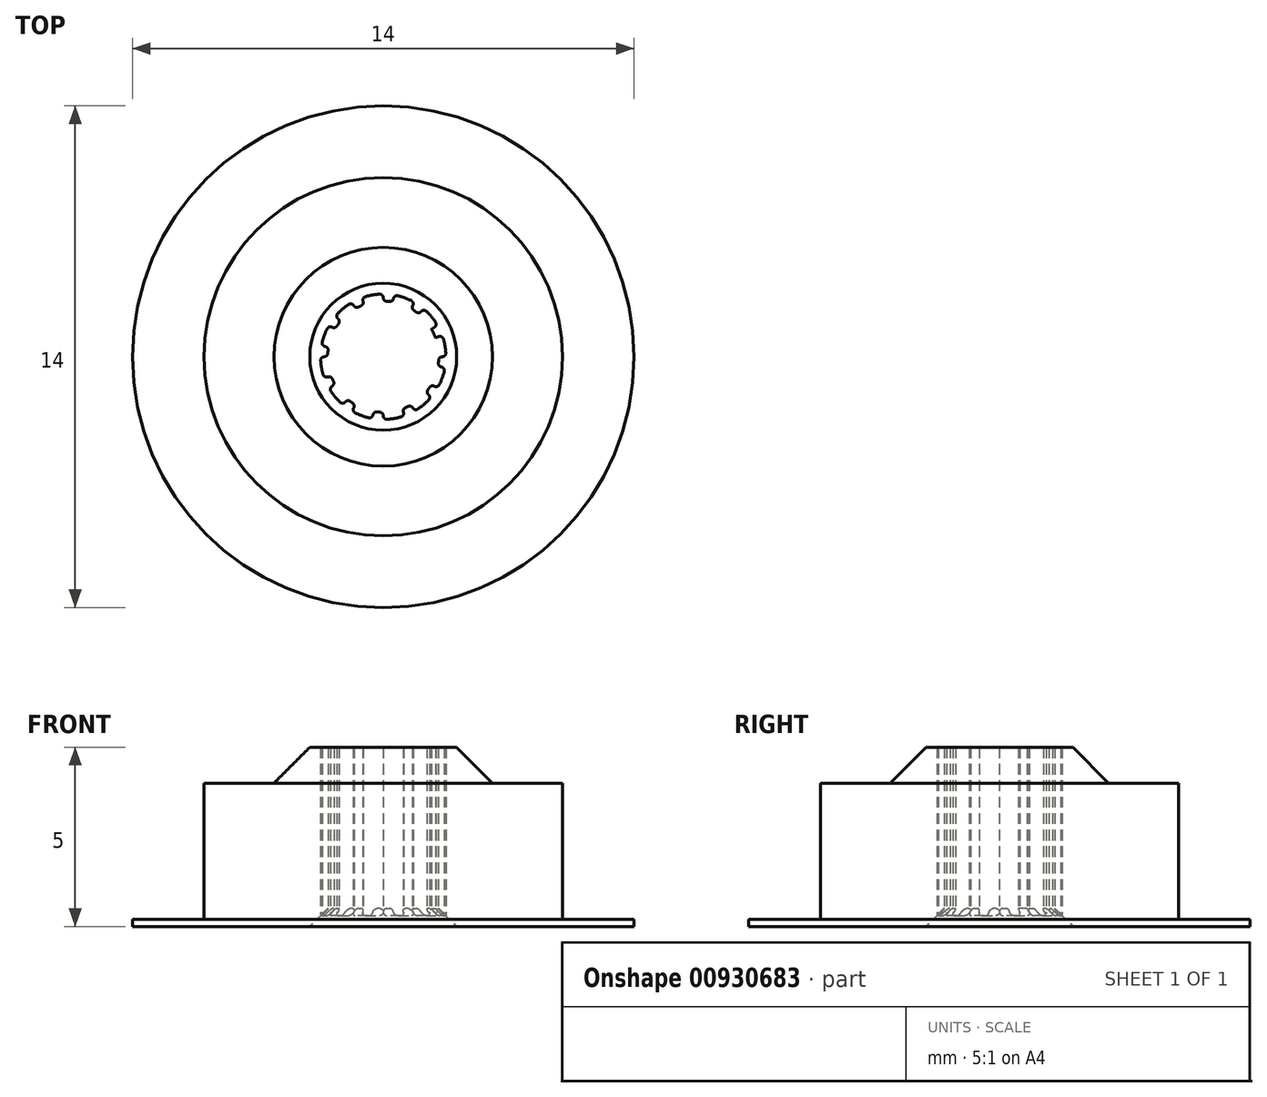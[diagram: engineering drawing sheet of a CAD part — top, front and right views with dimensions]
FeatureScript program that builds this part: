
annotation { "Feature Type Name" : "Feature", "Feature Type Description" : "" }
export const myFeature = defineFeature(function(context is Context, id is Id, definition is map)
    precondition{}
    {
        {
            var Q0;
            Q0=qCreatedBy(makeId("Front.planeOp"),FACE);
            var sketch = newSketch(context, id + "F0", { "sketchPlane" : qUnion([Q0])});
            skLineSegment(sketch, "E0", {"start": v(0, 0) * mm, "end": v(0, 10) * mm, "construction": true});
            skLineSegment(sketch, "E1", {"start": v(1.55, 5) * mm, "end": v(2.05, 5) * mm});
            skLineSegment(sketch, "E2", {"start": v(2.05, 5) * mm, "end": v(3.05, 4) * mm});
            skLineSegment(sketch, "E3", {"start": v(3.05, 4) * mm, "end": v(5, 4) * mm});
            skLineSegment(sketch, "E4", {"start": v(5, 4) * mm, "end": v(5, 0) * mm});
            skLineSegment(sketch, "E5", {"start": v(5, 0) * mm, "end": v(2.05, 0) * mm});
            skLineSegment(sketch, "E6", {"start": v(1.55, 0.5) * mm, "end": v(1.55, 5) * mm});
            skLineSegment(sketch, "E7", {"start": v(2.05, 0) * mm, "end": v(1.55, 0.5) * mm});
            skSolve(sketch);
        }
        {
            var Q0;
            Q0=qSketchRegion(id+"F0",true);
            var Q1;
            Q1=sQuery(id+"F0.wireOp",EDGE,"E0");
            revolve(context, id + "F1", {"entities" : qUnion([Q0]), "axis" : qUnion([Q1]), "revolveType" : RevolveType.FULL});
        }
        {
            var Q0;
            Q0=makeQuery(id+"F1.opRevolve","SWEPT_FACE",FACE,{"disambiguationData":[OSD([sQuery(id+"F0.wireOp",EDGE,"E5")])]});
            var sketch = newSketch(context, id + "F2", { "sketchPlane" : qUnion([Q0])});
            skCircle(sketch, "E8", {"center": v(0, 0) * mm, "radius": 1.5 * mm, "construction": true});
            skArc(sketch, "E9", {"start": v(-1.72, -0.3) * mm, "mid": v(-1.64, -0.6) * mm, "end": v(-1.52, -0.87) * mm});
            skArc(sketch, "E10", {"start": v(-1.34, -0.78) * mm, "mid": v(-1.27, -0.89) * mm, "end": v(-1.19, -1) * mm});
            skLineSegment(sketch, "E11", {"start": v(-1.75, 0) * mm, "end": v(-1.55, 0) * mm});
            skLineSegment(sketch, "E12", {"start": v(-1.72, -0.3) * mm, "end": v(-1.53, -0.27) * mm});
            skLineSegment(sketch, "E13.1.0", {"start": v(-1.34, -1.12) * mm, "end": v(-1.19, -1) * mm});
            skLineSegment(sketch, "E13.1.1", {"start": v(-1.52, -0.88) * mm, "end": v(-1.34, -0.78) * mm});
            skLineSegment(sketch, "E13.2.0", {"start": v(-0.6, -1.64) * mm, "end": v(-0.53, -1.46) * mm});
            skLineSegment(sketch, "E13.2.1", {"start": v(-0.88, -1.52) * mm, "end": v(-0.78, -1.34) * mm});
            skLineSegment(sketch, "E13.3.0", {"start": v(0.3, -1.72) * mm, "end": v(0.27, -1.53) * mm});
            skLineSegment(sketch, "E13.3.1", {"start": v(0, -1.75) * mm, "end": v(0, -1.55) * mm});
            skLineSegment(sketch, "E13.4.0", {"start": v(1.12, -1.34) * mm, "end": v(1, -1.19) * mm});
            skLineSegment(sketch, "E13.4.1", {"start": v(0.88, -1.52) * mm, "end": v(0.78, -1.34) * mm});
            skLineSegment(sketch, "E13.5.0", {"start": v(1.64, -0.6) * mm, "end": v(1.46, -0.53) * mm});
            skLineSegment(sketch, "E13.5.1", {"start": v(1.52, -0.88) * mm, "end": v(1.34, -0.78) * mm});
            skLineSegment(sketch, "E13.6.0", {"start": v(1.72, 0.3) * mm, "end": v(1.53, 0.27) * mm});
            skLineSegment(sketch, "E13.6.1", {"start": v(1.75, 0) * mm, "end": v(1.55, 0) * mm});
            skLineSegment(sketch, "E13.7.0", {"start": v(1.34, 1.12) * mm, "end": v(1.19, 1) * mm});
            skLineSegment(sketch, "E13.7.1", {"start": v(1.52, 0.88) * mm, "end": v(1.34, 0.78) * mm});
            skLineSegment(sketch, "E13.8.0", {"start": v(0.6, 1.64) * mm, "end": v(0.53, 1.46) * mm});
            skLineSegment(sketch, "E13.8.1", {"start": v(0.88, 1.52) * mm, "end": v(0.78, 1.34) * mm});
            skLineSegment(sketch, "E13.9.0", {"start": v(-0.3, 1.72) * mm, "end": v(-0.27, 1.53) * mm});
            skLineSegment(sketch, "E13.9.1", {"start": v(0, 1.75) * mm, "end": v(0, 1.55) * mm});
            skLineSegment(sketch, "E13.10.0", {"start": v(-1.12, 1.34) * mm, "end": v(-1, 1.19) * mm});
            skLineSegment(sketch, "E13.10.1", {"start": v(-0.87, 1.52) * mm, "end": v(-0.77, 1.34) * mm});
            skLineSegment(sketch, "E13.11.0", {"start": v(-1.64, 0.6) * mm, "end": v(-1.46, 0.53) * mm});
            skLineSegment(sketch, "E13.11.1", {"start": v(-1.52, 0.88) * mm, "end": v(-1.34, 0.78) * mm});
            skArc(sketch, "E14.trimOffspring", {"start": v(-1.34, -1.12) * mm, "mid": v(-1.12, -1.34) * mm, "end": v(-0.88, -1.52) * mm});
            skArc(sketch, "E15.trimOffspring", {"start": v(-0.6, -1.64) * mm, "mid": v(-0.3, -1.72) * mm, "end": v(0, -1.75) * mm});
            skArc(sketch, "E16.trimOffspring", {"start": v(0.3, -1.72) * mm, "mid": v(0.6, -1.64) * mm, "end": v(0.87, -1.52) * mm});
            skArc(sketch, "E17.trimOffspring", {"start": v(1.12, -1.34) * mm, "mid": v(1.34, -1.12) * mm, "end": v(1.52, -0.88) * mm});
            skArc(sketch, "E18.trimOffspring", {"start": v(1.64, -0.6) * mm, "mid": v(1.72, -0.3) * mm, "end": v(1.75, 0) * mm});
            skArc(sketch, "E19.trimOffspring", {"start": v(1.72, 0.3) * mm, "mid": v(1.64, 0.6) * mm, "end": v(1.52, 0.87) * mm});
            skArc(sketch, "E20.trimOffspring", {"start": v(1.34, 1.12) * mm, "mid": v(1.12, 1.34) * mm, "end": v(0.88, 1.52) * mm});
            skArc(sketch, "E21.trimOffspring", {"start": v(0.6, 1.64) * mm, "mid": v(0.3, 1.72) * mm, "end": v(0, 1.75) * mm});
            skArc(sketch, "E22.trimOffspring", {"start": v(-0.3, 1.72) * mm, "mid": v(-0.6, 1.64) * mm, "end": v(-0.87, 1.52) * mm});
            skArc(sketch, "E23.trimOffspring", {"start": v(-1.12, 1.34) * mm, "mid": v(-1.34, 1.12) * mm, "end": v(-1.52, 0.88) * mm});
            skArc(sketch, "E24.trimOffspring", {"start": v(-1.64, 0.6) * mm, "mid": v(-1.72, 0.3) * mm, "end": v(-1.75, 0) * mm});
            skArc(sketch, "E25.trimOffspring", {"start": v(-0.78, -1.34) * mm, "mid": v(-0.66, -1.4) * mm, "end": v(-0.53, -1.46) * mm});
            skArc(sketch, "E26.trimOffspring", {"start": v(0, -1.55) * mm, "mid": v(0.14, -1.54) * mm, "end": v(0.27, -1.53) * mm});
            skArc(sketch, "E27.trimOffspring", {"start": v(0.77, -1.34) * mm, "mid": v(0.89, -1.27) * mm, "end": v(1, -1.19) * mm});
            skArc(sketch, "E28.trimOffspring", {"start": v(1.34, -0.78) * mm, "mid": v(1.4, -0.66) * mm, "end": v(1.46, -0.53) * mm});
            skArc(sketch, "E29.trimOffspring", {"start": v(1.55, 0) * mm, "mid": v(1.54, 0.14) * mm, "end": v(1.53, 0.27) * mm});
            skArc(sketch, "E30.trimOffspring", {"start": v(1.34, 0.77) * mm, "mid": v(1.27, 0.89) * mm, "end": v(1.19, 1) * mm});
            skArc(sketch, "E31.trimOffspring", {"start": v(0.78, 1.34) * mm, "mid": v(0.66, 1.4) * mm, "end": v(0.53, 1.46) * mm});
            skArc(sketch, "E32.trimOffspring", {"start": v(0, 1.55) * mm, "mid": v(-0.14, 1.54) * mm, "end": v(-0.27, 1.53) * mm});
            skArc(sketch, "E33.trimOffspring", {"start": v(-0.77, 1.34) * mm, "mid": v(-0.89, 1.27) * mm, "end": v(-1, 1.19) * mm});
            skArc(sketch, "E34.trimOffspring", {"start": v(-1.34, 0.78) * mm, "mid": v(-1.4, 0.66) * mm, "end": v(-1.46, 0.53) * mm});
            skArc(sketch, "E35.trimOffspring", {"start": v(-1.55, 0) * mm, "mid": v(-1.54, -0.14) * mm, "end": v(-1.53, -0.27) * mm});
            skSolve(sketch);
        }
        {
            var Q0;
            Q0=qSketchRegion(id+"F2",true);
            var Q1;
            Q1=makeQuery(id+"F1.opRevolve","SWEPT_FACE",FACE,{"disambiguationData":[OSD([sQuery(id+"F0.wireOp",EDGE,"E1")])]});
            extrude(context, id + "F3", {"entities" : qUnion([Q0]), "operationType" : NewBodyOperationType.REMOVE, "endBound" : BoundingType.UP_TO_SURFACE, "oppositeDirection" : true, "depth" : 25 * mm, "endBoundEntityFace" : qUnion([Q1]), "offsetDistance" : 25 * mm});
        }
        {
            var Q0;
            Q0=makeQuery(id+"F3.boolean.opBoolean","COPY",EDGE,{"derivedFrom":makeQuery(id+"F3.opExtrude","SWEPT_EDGE",EDGE,{"disambiguationData":[OSD([sQuery(id+"F2.wireOp",EDGE,"E13.4.0"),sQuery(id+"F2.wireOp",EDGE,"E17.trimOffspring")])]})});
            var Q1;
            Q1=makeQuery(id+"F3.boolean.opBoolean","COPY",EDGE,{"derivedFrom":makeQuery(id+"F3.opExtrude","SWEPT_EDGE",EDGE,{"disambiguationData":[OSD([sQuery(id+"F2.wireOp",EDGE,"E13.4.1"),sQuery(id+"F2.wireOp",EDGE,"E16.trimOffspring")])]})});
            var Q2;
            Q2=makeQuery(id+"F3.boolean.opBoolean","COPY",EDGE,{"derivedFrom":makeQuery(id+"F3.opExtrude","SWEPT_EDGE",EDGE,{"disambiguationData":[OSD([sQuery(id+"F2.wireOp",EDGE,"E13.4.0"),sQuery(id+"F2.wireOp",EDGE,"E27.trimOffspring")])]})});
            var Q3;
            Q3=makeQuery(id+"F3.boolean.opBoolean","COPY",EDGE,{"derivedFrom":makeQuery(id+"F3.opExtrude","SWEPT_EDGE",EDGE,{"disambiguationData":[OSD([sQuery(id+"F2.wireOp",EDGE,"E13.4.1"),sQuery(id+"F2.wireOp",EDGE,"E27.trimOffspring")])]})});
            var Q4;
            Q4=makeQuery(id+"F3.boolean.opBoolean","COPY",EDGE,{"derivedFrom":makeQuery(id+"F3.opExtrude","SWEPT_EDGE",EDGE,{"disambiguationData":[OSD([sQuery(id+"F2.wireOp",EDGE,"E13.3.0"),sQuery(id+"F2.wireOp",EDGE,"E16.trimOffspring")])]})});
            var Q5;
            Q5=makeQuery(id+"F3.boolean.opBoolean","COPY",EDGE,{"derivedFrom":makeQuery(id+"F3.opExtrude","SWEPT_EDGE",EDGE,{"disambiguationData":[OSD([sQuery(id+"F2.wireOp",EDGE,"E13.3.0"),sQuery(id+"F2.wireOp",EDGE,"E26.trimOffspring")])]})});
            var Q6;
            Q6=makeQuery(id+"F3.boolean.opBoolean","COPY",EDGE,{"derivedFrom":makeQuery(id+"F3.opExtrude","SWEPT_EDGE",EDGE,{"disambiguationData":[OSD([sQuery(id+"F2.wireOp",EDGE,"E13.3.1"),sQuery(id+"F2.wireOp",EDGE,"E26.trimOffspring")])]})});
            var Q7;
            Q7=makeQuery(id+"F3.boolean.opBoolean","COPY",EDGE,{"derivedFrom":makeQuery(id+"F3.opExtrude","SWEPT_EDGE",EDGE,{"disambiguationData":[OSD([sQuery(id+"F2.wireOp",EDGE,"E13.3.1"),sQuery(id+"F2.wireOp",EDGE,"E15.trimOffspring")])]})});
            var Q8;
            Q8=makeQuery(id+"F3.boolean.opBoolean","COPY",EDGE,{"derivedFrom":makeQuery(id+"F3.opExtrude","SWEPT_EDGE",EDGE,{"disambiguationData":[OSD([sQuery(id+"F2.wireOp",EDGE,"E13.2.0"),sQuery(id+"F2.wireOp",EDGE,"E15.trimOffspring")])]})});
            var Q9;
            Q9=makeQuery(id+"F3.boolean.opBoolean","COPY",EDGE,{"derivedFrom":makeQuery(id+"F3.opExtrude","SWEPT_EDGE",EDGE,{"disambiguationData":[OSD([sQuery(id+"F2.wireOp",EDGE,"E13.2.0"),sQuery(id+"F2.wireOp",EDGE,"E25.trimOffspring")])]})});
            var Q10;
            Q10=makeQuery(id+"F3.boolean.opBoolean","COPY",EDGE,{"derivedFrom":makeQuery(id+"F3.opExtrude","SWEPT_EDGE",EDGE,{"disambiguationData":[OSD([sQuery(id+"F2.wireOp",EDGE,"E13.2.1"),sQuery(id+"F2.wireOp",EDGE,"E25.trimOffspring")])]})});
            var Q11;
            Q11=makeQuery(id+"F3.boolean.opBoolean","COPY",EDGE,{"derivedFrom":makeQuery(id+"F3.opExtrude","SWEPT_EDGE",EDGE,{"disambiguationData":[OSD([sQuery(id+"F2.wireOp",EDGE,"E13.2.1"),sQuery(id+"F2.wireOp",EDGE,"E14.trimOffspring")])]})});
            var Q12;
            Q12=makeQuery(id+"F3.boolean.opBoolean","COPY",EDGE,{"derivedFrom":makeQuery(id+"F3.opExtrude","SWEPT_EDGE",EDGE,{"disambiguationData":[OSD([sQuery(id+"F2.wireOp",EDGE,"E13.1.0"),sQuery(id+"F2.wireOp",EDGE,"E14.trimOffspring")])]})});
            var Q13;
            Q13=makeQuery(id+"F3.boolean.opBoolean","COPY",EDGE,{"derivedFrom":makeQuery(id+"F3.opExtrude","SWEPT_EDGE",EDGE,{"disambiguationData":[OSD([sQuery(id+"F2.wireOp",EDGE,"E10"),sQuery(id+"F2.wireOp",EDGE,"E13.1.0")])]})});
            var Q14;
            Q14=makeQuery(id+"F3.boolean.opBoolean","COPY",EDGE,{"derivedFrom":makeQuery(id+"F3.opExtrude","SWEPT_EDGE",EDGE,{"disambiguationData":[OSD([sQuery(id+"F2.wireOp",EDGE,"E10"),sQuery(id+"F2.wireOp",EDGE,"E13.1.1")])]})});
            var Q15;
            Q15=makeQuery(id+"F3.boolean.opBoolean","COPY",EDGE,{"derivedFrom":makeQuery(id+"F3.opExtrude","SWEPT_EDGE",EDGE,{"disambiguationData":[OSD([sQuery(id+"F2.wireOp",EDGE,"E9"),sQuery(id+"F2.wireOp",EDGE,"E13.1.1")])]})});
            var Q16;
            Q16=makeQuery(id+"F3.boolean.opBoolean","COPY",EDGE,{"derivedFrom":makeQuery(id+"F3.opExtrude","SWEPT_EDGE",EDGE,{"disambiguationData":[OSD([sQuery(id+"F2.wireOp",EDGE,"E9"),sQuery(id+"F2.wireOp",EDGE,"E12")])]})});
            var Q17;
            Q17=makeQuery(id+"F3.boolean.opBoolean","COPY",EDGE,{"derivedFrom":makeQuery(id+"F3.opExtrude","SWEPT_EDGE",EDGE,{"disambiguationData":[OSD([sQuery(id+"F2.wireOp",EDGE,"E12"),sQuery(id+"F2.wireOp",EDGE,"E35.trimOffspring")])]})});
            var Q18;
            Q18=makeQuery(id+"F3.boolean.opBoolean","COPY",EDGE,{"derivedFrom":makeQuery(id+"F3.opExtrude","SWEPT_EDGE",EDGE,{"disambiguationData":[OSD([sQuery(id+"F2.wireOp",EDGE,"E11"),sQuery(id+"F2.wireOp",EDGE,"E35.trimOffspring")])]})});
            var Q19;
            Q19=makeQuery(id+"F3.boolean.opBoolean","COPY",EDGE,{"derivedFrom":makeQuery(id+"F3.opExtrude","SWEPT_EDGE",EDGE,{"disambiguationData":[OSD([sQuery(id+"F2.wireOp",EDGE,"E11"),sQuery(id+"F2.wireOp",EDGE,"E24.trimOffspring")])]})});
            var Q20;
            Q20=makeQuery(id+"F3.boolean.opBoolean","COPY",EDGE,{"derivedFrom":makeQuery(id+"F3.opExtrude","SWEPT_EDGE",EDGE,{"disambiguationData":[OSD([sQuery(id+"F2.wireOp",EDGE,"E13.11.0"),sQuery(id+"F2.wireOp",EDGE,"E24.trimOffspring")])]})});
            var Q21;
            Q21=makeQuery(id+"F3.boolean.opBoolean","COPY",EDGE,{"derivedFrom":makeQuery(id+"F3.opExtrude","SWEPT_EDGE",EDGE,{"disambiguationData":[OSD([sQuery(id+"F2.wireOp",EDGE,"E13.11.0"),sQuery(id+"F2.wireOp",EDGE,"E34.trimOffspring")])]})});
            var Q22;
            Q22=makeQuery(id+"F3.boolean.opBoolean","COPY",EDGE,{"derivedFrom":makeQuery(id+"F3.opExtrude","SWEPT_EDGE",EDGE,{"disambiguationData":[OSD([sQuery(id+"F2.wireOp",EDGE,"E13.11.1"),sQuery(id+"F2.wireOp",EDGE,"E34.trimOffspring")])]})});
            var Q23;
            Q23=makeQuery(id+"F3.boolean.opBoolean","COPY",EDGE,{"derivedFrom":makeQuery(id+"F3.opExtrude","SWEPT_EDGE",EDGE,{"disambiguationData":[OSD([sQuery(id+"F2.wireOp",EDGE,"E13.11.1"),sQuery(id+"F2.wireOp",EDGE,"E23.trimOffspring")])]})});
            var Q24;
            Q24=makeQuery(id+"F3.boolean.opBoolean","COPY",EDGE,{"derivedFrom":makeQuery(id+"F3.opExtrude","SWEPT_EDGE",EDGE,{"disambiguationData":[OSD([sQuery(id+"F2.wireOp",EDGE,"E13.10.0"),sQuery(id+"F2.wireOp",EDGE,"E23.trimOffspring")])]})});
            var Q25;
            Q25=makeQuery(id+"F3.boolean.opBoolean","COPY",EDGE,{"derivedFrom":makeQuery(id+"F3.opExtrude","SWEPT_EDGE",EDGE,{"disambiguationData":[OSD([sQuery(id+"F2.wireOp",EDGE,"E13.10.0"),sQuery(id+"F2.wireOp",EDGE,"E33.trimOffspring")])]})});
            var Q26;
            Q26=makeQuery(id+"F3.boolean.opBoolean","COPY",EDGE,{"derivedFrom":makeQuery(id+"F3.opExtrude","SWEPT_EDGE",EDGE,{"disambiguationData":[OSD([sQuery(id+"F2.wireOp",EDGE,"E13.10.1"),sQuery(id+"F2.wireOp",EDGE,"E33.trimOffspring")])]})});
            var Q27;
            Q27=makeQuery(id+"F3.boolean.opBoolean","COPY",EDGE,{"derivedFrom":makeQuery(id+"F3.opExtrude","SWEPT_EDGE",EDGE,{"disambiguationData":[OSD([sQuery(id+"F2.wireOp",EDGE,"E13.10.1"),sQuery(id+"F2.wireOp",EDGE,"E22.trimOffspring")])]})});
            var Q28;
            Q28=makeQuery(id+"F3.boolean.opBoolean","COPY",EDGE,{"derivedFrom":makeQuery(id+"F3.opExtrude","SWEPT_EDGE",EDGE,{"disambiguationData":[OSD([sQuery(id+"F2.wireOp",EDGE,"E13.9.0"),sQuery(id+"F2.wireOp",EDGE,"E22.trimOffspring")])]})});
            var Q29;
            Q29=makeQuery(id+"F3.boolean.opBoolean","COPY",EDGE,{"derivedFrom":makeQuery(id+"F3.opExtrude","SWEPT_EDGE",EDGE,{"disambiguationData":[OSD([sQuery(id+"F2.wireOp",EDGE,"E13.9.0"),sQuery(id+"F2.wireOp",EDGE,"E32.trimOffspring")])]})});
            var Q30;
            Q30=makeQuery(id+"F3.boolean.opBoolean","COPY",EDGE,{"derivedFrom":makeQuery(id+"F3.opExtrude","SWEPT_EDGE",EDGE,{"disambiguationData":[OSD([sQuery(id+"F2.wireOp",EDGE,"E13.9.1"),sQuery(id+"F2.wireOp",EDGE,"E32.trimOffspring")])]})});
            var Q31;
            Q31=makeQuery(id+"F3.boolean.opBoolean","COPY",EDGE,{"derivedFrom":makeQuery(id+"F3.opExtrude","SWEPT_EDGE",EDGE,{"disambiguationData":[OSD([sQuery(id+"F2.wireOp",EDGE,"E13.9.1"),sQuery(id+"F2.wireOp",EDGE,"E21.trimOffspring")])]})});
            var Q32;
            Q32=makeQuery(id+"F3.boolean.opBoolean","COPY",EDGE,{"derivedFrom":makeQuery(id+"F3.opExtrude","SWEPT_EDGE",EDGE,{"disambiguationData":[OSD([sQuery(id+"F2.wireOp",EDGE,"E13.8.0"),sQuery(id+"F2.wireOp",EDGE,"E21.trimOffspring")])]})});
            var Q33;
            Q33=makeQuery(id+"F3.boolean.opBoolean","COPY",EDGE,{"derivedFrom":makeQuery(id+"F3.opExtrude","SWEPT_EDGE",EDGE,{"disambiguationData":[OSD([sQuery(id+"F2.wireOp",EDGE,"E13.8.0"),sQuery(id+"F2.wireOp",EDGE,"E31.trimOffspring")])]})});
            var Q34;
            Q34=makeQuery(id+"F3.boolean.opBoolean","COPY",EDGE,{"derivedFrom":makeQuery(id+"F3.opExtrude","SWEPT_EDGE",EDGE,{"disambiguationData":[OSD([sQuery(id+"F2.wireOp",EDGE,"E13.8.1"),sQuery(id+"F2.wireOp",EDGE,"E31.trimOffspring")])]})});
            var Q35;
            Q35=makeQuery(id+"F3.boolean.opBoolean","COPY",EDGE,{"derivedFrom":makeQuery(id+"F3.opExtrude","SWEPT_EDGE",EDGE,{"disambiguationData":[OSD([sQuery(id+"F2.wireOp",EDGE,"E13.8.1"),sQuery(id+"F2.wireOp",EDGE,"E20.trimOffspring")])]})});
            var Q36;
            Q36=makeQuery(id+"F3.boolean.opBoolean","COPY",EDGE,{"derivedFrom":makeQuery(id+"F3.opExtrude","SWEPT_EDGE",EDGE,{"disambiguationData":[OSD([sQuery(id+"F2.wireOp",EDGE,"E13.7.0"),sQuery(id+"F2.wireOp",EDGE,"E20.trimOffspring")])]})});
            var Q37;
            Q37=makeQuery(id+"F3.boolean.opBoolean","COPY",EDGE,{"derivedFrom":makeQuery(id+"F3.opExtrude","SWEPT_EDGE",EDGE,{"disambiguationData":[OSD([sQuery(id+"F2.wireOp",EDGE,"E13.7.0"),sQuery(id+"F2.wireOp",EDGE,"E30.trimOffspring")])]})});
            var Q38;
            Q38=makeQuery(id+"F3.boolean.opBoolean","COPY",EDGE,{"derivedFrom":makeQuery(id+"F3.opExtrude","SWEPT_EDGE",EDGE,{"disambiguationData":[OSD([sQuery(id+"F2.wireOp",EDGE,"E13.7.1"),sQuery(id+"F2.wireOp",EDGE,"E30.trimOffspring")])]})});
            var Q39;
            Q39=makeQuery(id+"F3.boolean.opBoolean","COPY",EDGE,{"derivedFrom":makeQuery(id+"F3.opExtrude","SWEPT_EDGE",EDGE,{"disambiguationData":[OSD([sQuery(id+"F2.wireOp",EDGE,"E13.7.1"),sQuery(id+"F2.wireOp",EDGE,"E19.trimOffspring")])]})});
            var Q40;
            Q40=makeQuery(id+"F3.boolean.opBoolean","COPY",EDGE,{"derivedFrom":makeQuery(id+"F3.opExtrude","SWEPT_EDGE",EDGE,{"disambiguationData":[OSD([sQuery(id+"F2.wireOp",EDGE,"E13.6.0"),sQuery(id+"F2.wireOp",EDGE,"E19.trimOffspring")])]})});
            var Q41;
            Q41=makeQuery(id+"F3.boolean.opBoolean","COPY",EDGE,{"derivedFrom":makeQuery(id+"F3.opExtrude","SWEPT_EDGE",EDGE,{"disambiguationData":[OSD([sQuery(id+"F2.wireOp",EDGE,"E13.6.0"),sQuery(id+"F2.wireOp",EDGE,"E29.trimOffspring")])]})});
            var Q42;
            Q42=makeQuery(id+"F3.boolean.opBoolean","COPY",EDGE,{"derivedFrom":makeQuery(id+"F3.opExtrude","SWEPT_EDGE",EDGE,{"disambiguationData":[OSD([sQuery(id+"F2.wireOp",EDGE,"E13.6.1"),sQuery(id+"F2.wireOp",EDGE,"E29.trimOffspring")])]})});
            var Q43;
            Q43=makeQuery(id+"F3.boolean.opBoolean","COPY",EDGE,{"derivedFrom":makeQuery(id+"F3.opExtrude","SWEPT_EDGE",EDGE,{"disambiguationData":[OSD([sQuery(id+"F2.wireOp",EDGE,"E13.6.1"),sQuery(id+"F2.wireOp",EDGE,"E18.trimOffspring")])]})});
            var Q44;
            Q44=makeQuery(id+"F3.boolean.opBoolean","COPY",EDGE,{"derivedFrom":makeQuery(id+"F3.opExtrude","SWEPT_EDGE",EDGE,{"disambiguationData":[OSD([sQuery(id+"F2.wireOp",EDGE,"E13.5.0"),sQuery(id+"F2.wireOp",EDGE,"E18.trimOffspring")])]})});
            var Q45;
            Q45=makeQuery(id+"F3.boolean.opBoolean","COPY",EDGE,{"derivedFrom":makeQuery(id+"F3.opExtrude","SWEPT_EDGE",EDGE,{"disambiguationData":[OSD([sQuery(id+"F2.wireOp",EDGE,"E13.5.0"),sQuery(id+"F2.wireOp",EDGE,"E28.trimOffspring")])]})});
            var Q46;
            Q46=makeQuery(id+"F3.boolean.opBoolean","COPY",EDGE,{"derivedFrom":makeQuery(id+"F3.opExtrude","SWEPT_EDGE",EDGE,{"disambiguationData":[OSD([sQuery(id+"F2.wireOp",EDGE,"E13.5.1"),sQuery(id+"F2.wireOp",EDGE,"E28.trimOffspring")])]})});
            var Q47;
            Q47=makeQuery(id+"F3.boolean.opBoolean","COPY",EDGE,{"derivedFrom":makeQuery(id+"F3.opExtrude","SWEPT_EDGE",EDGE,{"disambiguationData":[OSD([sQuery(id+"F2.wireOp",EDGE,"E13.5.1"),sQuery(id+"F2.wireOp",EDGE,"E17.trimOffspring")])]})});
            fillet(context, id + "F4", {"entities" : qUnion([Q0, Q1, Q2, Q3, Q4, Q5, Q6, Q7, Q8, Q9, Q10, Q11, Q12, Q13, Q14, Q15, Q16, Q17, Q18, Q19, Q20, Q21, Q22, Q23, Q24, Q25, Q26, Q27, Q28, Q29, Q30, Q31, Q32, Q33, Q34, Q35, Q36, Q37, Q38, Q39, Q40, Q41, Q42, Q43, Q44, Q45, Q46, Q47]), "radius" : 0.1 * mm, "tangentPropagation" : true, "allowEdgeOverflow" : false});
        }
        {
            var Q0;
            Q0=qCreatedBy(makeId("Top.planeOp"),FACE);
            var sketch = newSketch(context, id + "F5", { "sketchPlane" : qUnion([Q0])});
            skCircle(sketch, "E36", {"center": v(0, 0) * mm, "radius": 7 * mm});
            skCircle(sketch, "E37", {"center": v(0, 0) * mm, "radius": 5 * mm});
            skSolve(sketch);
        }
        {
            var Q0;
            Q0=qSketchRegion(id+"F5",true);
            extrude(context, id + "F6", {"entities" : qUnion([Q0]), "operationType" : NewBodyOperationType.ADD, "depth" : 0.2 * mm, "offsetDistance" : 25 * mm});
        }
    });
